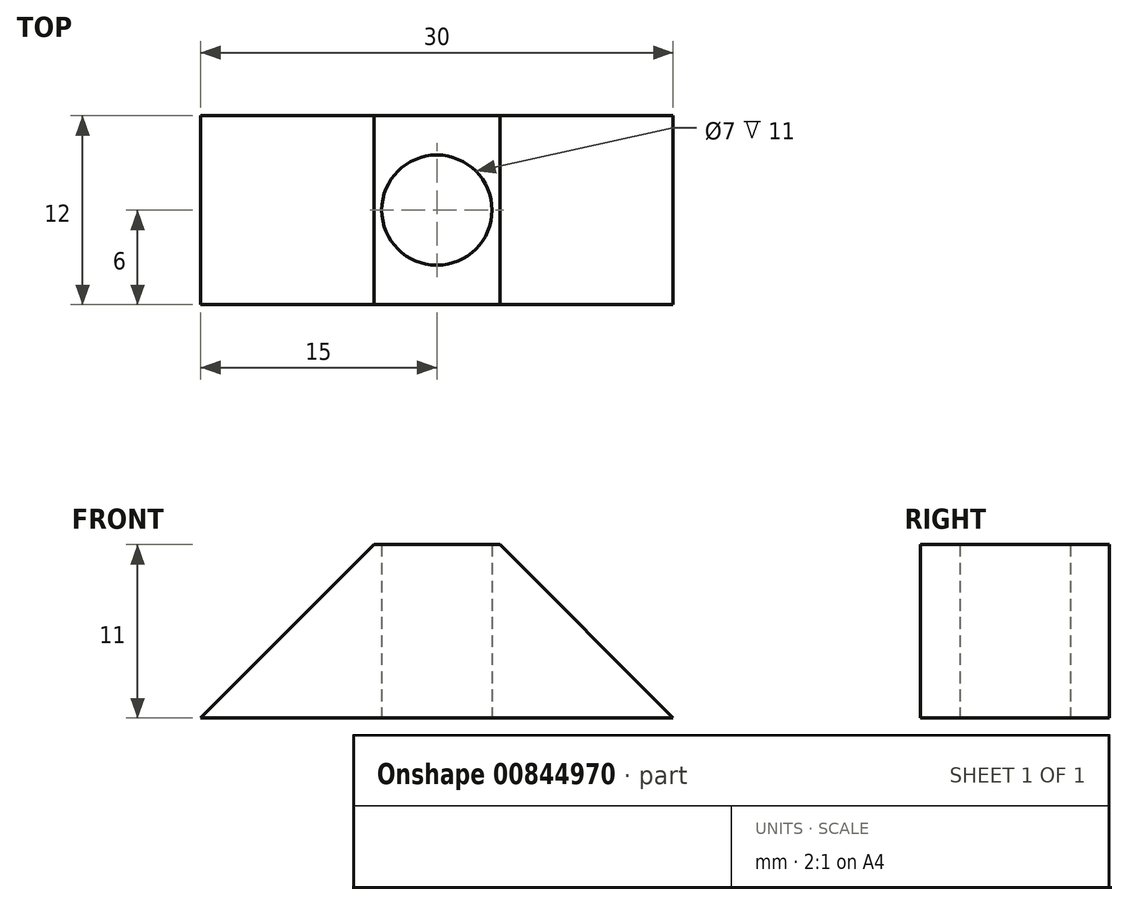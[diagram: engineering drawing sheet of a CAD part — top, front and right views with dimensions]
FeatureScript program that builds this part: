
annotation { "Feature Type Name" : "Feature", "Feature Type Description" : "" }
export const myFeature = defineFeature(function(context is Context, id is Id, definition is map)
    precondition{}
    {
        {
            var Q0;
            Q0=qCreatedBy(makeId("Front.planeOp"),FACE);
            var sketch = newSketch(context, id + "F0", { "sketchPlane" : qUnion([Q0])});
            skLineSegment(sketch, "E0", {"start": v(0, 0) * mm, "end": v(30, 0) * mm});
            skLineSegment(sketch, "E1", {"start": v(30, 0) * mm, "end": v(19, 11) * mm});
            skLineSegment(sketch, "E2", {"start": v(11, 11) * mm, "end": v(0, 0) * mm});
            skLineSegment(sketch, "E3", {"start": v(11, 11) * mm, "end": v(19, 11) * mm});
            skSolve(sketch);
        }
        {
            var Q0;
            Q0 = qSketchRegion(id + "F0", true);
            extrude(context, id + "F1", {"entities" : qUnion([Q0]), "depth" : 12 * mm, "offsetDistance" : 25 * mm});
        }
        {
            var Q0;
            Q0=makeQuery(id+"F1.opExtrude","SWEPT_FACE",FACE,{"disambiguationData":[OSD([sQuery(id+"F0.wireOp",EDGE,"E0")])]});
            var sketch = newSketch(context, id + "F2", { "sketchPlane" : qUnion([Q0])});
            skCircle(sketch, "E4", {"center": v(15, 6) * mm, "radius": 3.5 * mm});
            skPoint(sketch, "E4.centerSnap0", {"position": v(0, 6) * mm});
            skPoint(sketch, "E4.centerSnap1", {"position": v(15, 0) * mm});
            skSolve(sketch);
        }
        {
            var Q0;
            Q0 = qSketchRegion(id + "F2", true);
            extrude(context, id + "F3", {"entities" : qUnion([Q0]), "operationType" : NewBodyOperationType.REMOVE, "endBound" : BoundingType.THROUGH_ALL, "oppositeDirection" : true, "depth" : 25 * mm, "offsetDistance" : 25 * mm});
        }
    });
